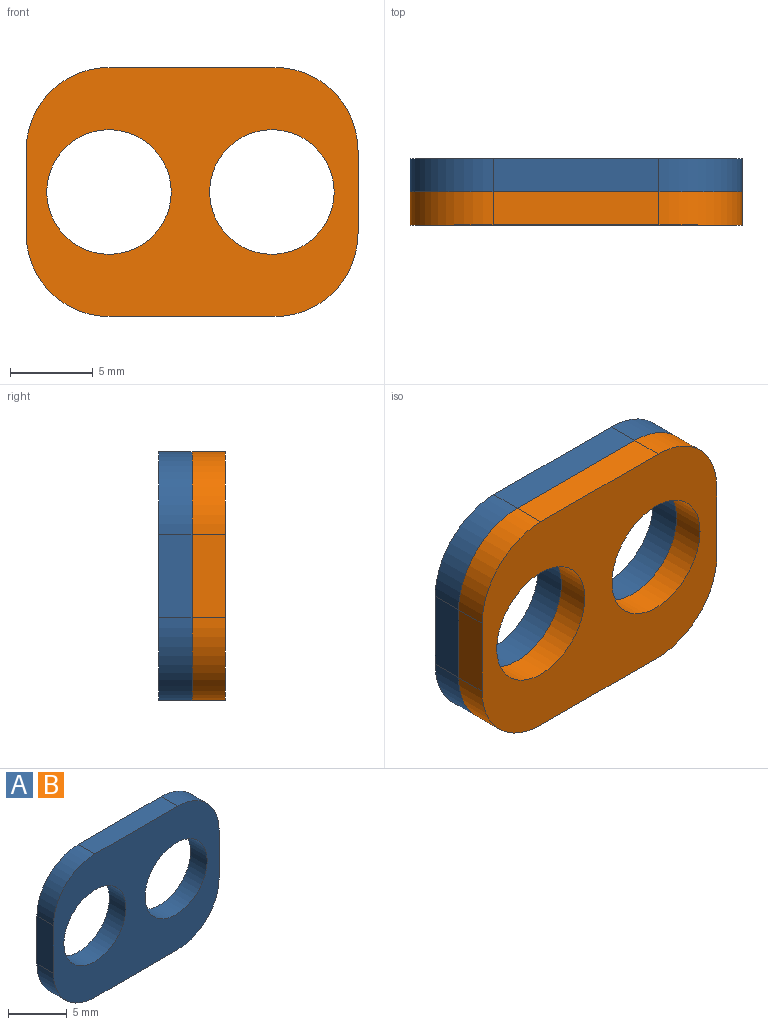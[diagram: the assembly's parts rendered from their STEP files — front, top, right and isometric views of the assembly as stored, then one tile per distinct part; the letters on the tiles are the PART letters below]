
ASSEMBLY  parts=2 mates=1
PART A: 12 faces, bbox 20x2x15 mm
  f0: plane 10x2mm, normal (0,0,-1), area 20mm2, adj f1,f9,f10,f11
  f1: cylinder r=5mm len=5mm, axis (0,1,0), area 15.7mm2, adj f0,f2,f10,f11
  f2: plane 5x2mm, normal (1,0,0), area 10mm2, adj f1,f3,f10,f11
  f3: cylinder r=5mm len=5mm, axis (0,1,0), area 15.7mm2, adj f2,f4,f10,f11
  f4: plane 10x2mm, normal (0,0,1), area 20mm2, adj f3,f5,f10,f11
  f5: cylinder r=5mm len=5mm, axis (0,1,0), area 15.7mm2, adj f4,f6,f10,f11
  f6: plane 5x2mm, normal (-1,0,0), area 10mm2, adj f5,f9,f10,f11
  f7: cylinder r=3.75mm len=7.5mm, axis (0,1,0), area 47.1mm2, adj f10,f11
  f8: cylinder r=3.75mm len=7.5mm, axis (0,1,0), area 47.1mm2, adj f10,f11
  f9: cylinder r=5mm len=5mm, axis (0,1,0), area 15.7mm2, adj f0,f6,f10,f11
  f10: plane 20x15mm, normal (0,-1,0), area 190.2mm2, adj f0,f1,f2,f3,f4,f5,f6,f7
  f11: plane 20x15mm, normal (0,1,0), area 190.2mm2, adj f0,f1,f2,f3,f4,f5,f6,f7
PART B: same geometry as A
PLACE A t=(-22.33,-12.53,-3.96)mm
PLACE B t=(-22.33,-14.53,-3.96)mm
MATE fastened A.f10 <-> B.f11  axis (0,-1,0) through (-22.29,-14.53,-3.96)mm
